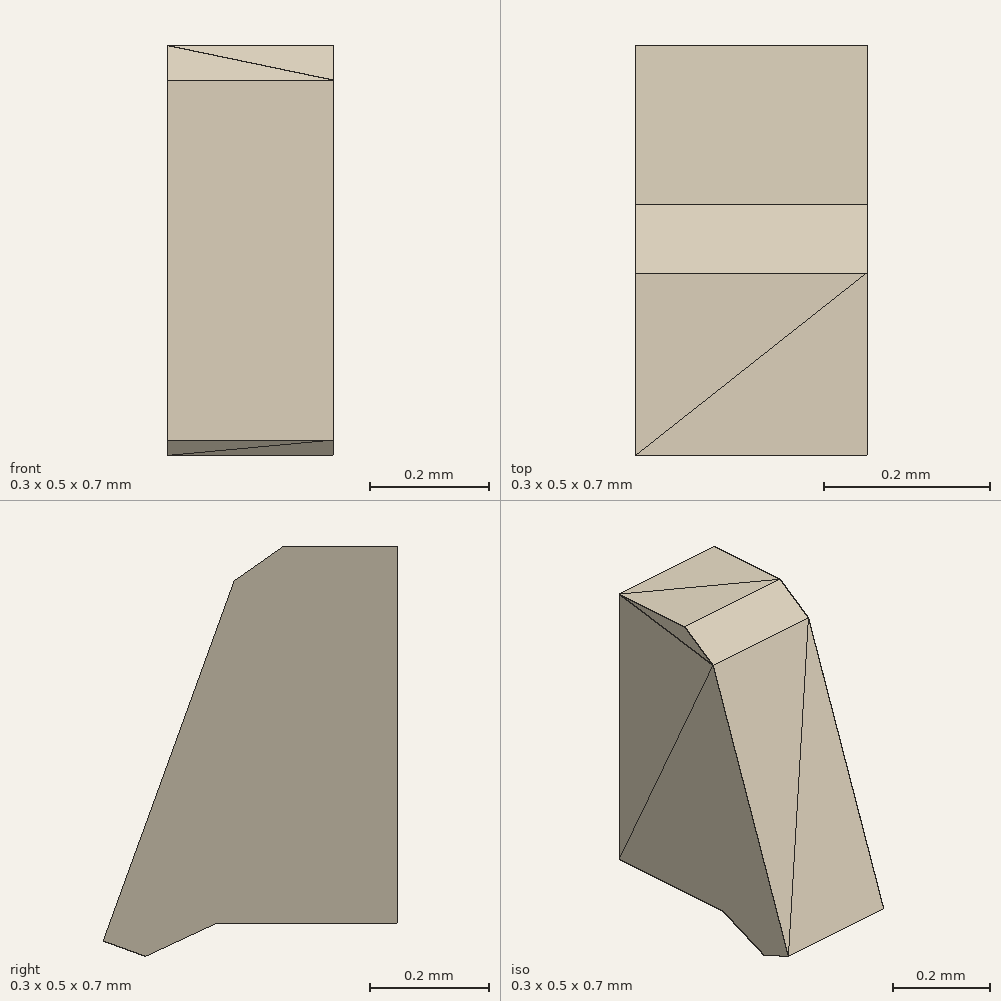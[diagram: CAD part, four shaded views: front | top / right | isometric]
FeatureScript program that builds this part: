
annotation { "Feature Type Name" : "Feature", "Feature Type Description" : "" }
export const myFeature = defineFeature(function(context is Context, id is Id, definition is map)
    precondition{}
    {
        {
            var Q0;
            Q0=qCreatedBy(makeId("Right.planeOp"),FACE);
            var sketch = newSketch(context, id + "F0", { "sketchPlane" : qUnion([Q0])});
            skLineSegment(sketch, "E0", {"start": v(0, 0.32) * mm, "end": v(0, -0.32) * mm});
            skLineSegment(sketch, "E1", {"start": v(-0.08, 0.57) * mm, "end": v(-0.08, -0.71) * mm, "construction": true});
            skLineSegment(sketch, "E2", {"start": v(0, 0.32) * mm, "end": v(-0.25, 0.32) * mm});
            skLineSegment(sketch, "E3", {"start": v(-0.5, -0.35) * mm, "end": v(-0.42, -0.37) * mm});
            skLineSegment(sketch, "E4", {"start": v(-0.3, -0.32) * mm, "end": v(0, -0.32) * mm});
            skLineSegment(sketch, "E5", {"start": v(-0.25, 0.32) * mm, "end": v(-0.5, -0.35) * mm});
            skLineSegment(sketch, "E6", {"start": v(-0.42, -0.37) * mm, "end": v(-0.3, -0.32) * mm});
            skLineSegment(sketch, "E7", {"start": v(-0.28, 0.26) * mm, "end": v(-0.2, 0.32) * mm});
            skLineSegment(sketch, "E8", {"start": v(-0.25, 0.32) * mm, "end": v(-0.23, 0.29) * mm, "construction": true});
            skSolve(sketch);
        }
        {
            var Q0;
            Q0=makeQuery(id+"F0.imprint","IMPRINT",FACE,{"disambiguationData":[TD([[makeQuery(id+"F0.imprint","IMPRINT",EDGE,{"derivedFrom":sQuery(id+"F0.wireOp",EDGE,"E0")}),-1.0]])]});
            extrude(context, id + "F1", {"entities" : qUnion([Q0]), "endBound" : BoundingType.SYMMETRIC, "depth" : 0.28 * mm});
        }
        {
            var Q0;
            Q0=makeQuery(id+"F1.opExtrude","SWEPT_BODY",BODY,{"disambiguationData":[OSD([sQuery(id+"F0.wireOp",EDGE,"E0"),sQuery(id+"F0.wireOp",EDGE,"E2"),sQuery(id+"F0.wireOp",EDGE,"E3"),sQuery(id+"F0.wireOp",EDGE,"E4"),sQuery(id+"F0.wireOp",EDGE,"E5"),sQuery(id+"F0.wireOp",EDGE,"E6"),sQuery(id+"F0.wireOp",EDGE,"E7")])]});
            transform(context, id + "F2", {"entities" : qUnion([Q0]), "transformType" : TransformType.COPY});
        }
    });
